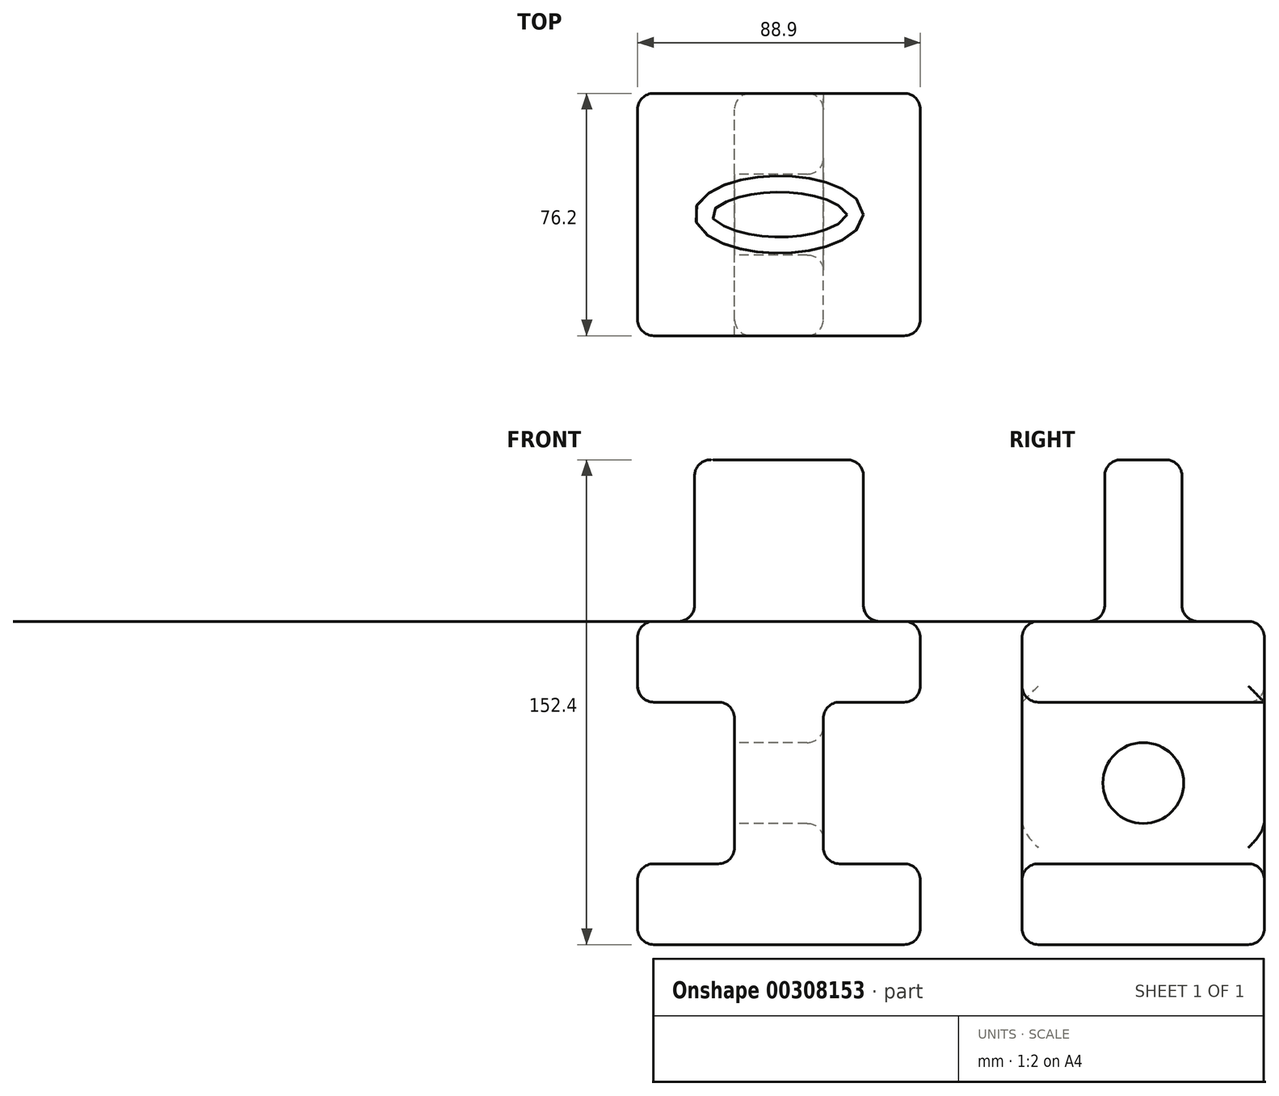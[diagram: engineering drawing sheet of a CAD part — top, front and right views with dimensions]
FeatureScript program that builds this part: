
annotation { "Feature Type Name" : "Feature", "Feature Type Description" : "" }
export const myFeature = defineFeature(function(context is Context, id is Id, definition is map)
    precondition{}
    {
        {
            var Q0;
            Q0=qCreatedBy(makeId("Front.planeOp"),FACE);
            var sketch = newSketch(context, id + "F0", { "sketchPlane" : qUnion([Q0])});
            skLineSegment(sketch, "E0", {"start": v(-56.03, -38.4) * mm, "end": v(32.87, -38.4) * mm});
            skLineSegment(sketch, "E1", {"start": v(32.87, -38.4) * mm, "end": v(32.87, -13) * mm});
            skLineSegment(sketch, "E2", {"start": v(32.87, -13) * mm, "end": v(2.39, -13) * mm});
            skLineSegment(sketch, "E3", {"start": v(2.39, -13) * mm, "end": v(2.39, 37.8) * mm});
            skLineSegment(sketch, "E4", {"start": v(2.39, 37.8) * mm, "end": v(32.87, 37.8) * mm});
            skLineSegment(sketch, "E5", {"start": v(32.87, 37.8) * mm, "end": v(32.87, 63.2) * mm});
            skLineSegment(sketch, "E6", {"start": v(32.87, 63.2) * mm, "end": v(-56.03, 63.2) * mm});
            skLineSegment(sketch, "E7", {"start": v(-56.03, 63.2) * mm, "end": v(-56.03, 37.8) * mm});
            skLineSegment(sketch, "E8", {"start": v(-56.03, 37.8) * mm, "end": v(-25.55, 37.8) * mm});
            skLineSegment(sketch, "E9", {"start": v(-25.55, 37.8) * mm, "end": v(-25.55, -13) * mm});
            skLineSegment(sketch, "E10", {"start": v(-25.55, -13) * mm, "end": v(-56.03, -13) * mm});
            skLineSegment(sketch, "E11", {"start": v(-56.03, -13) * mm, "end": v(-56.03, -38.4) * mm});
            skSolve(sketch);
        }
        {
            var Q0;
            Q0=makeQuery(id+"F0.imprint","IMPRINT",FACE,{"disambiguationData":[TD([[makeQuery(id+"F0.imprint","IMPRINT",EDGE,{"derivedFrom":sQuery(id+"F0.wireOp",EDGE,"E0")}),1.0]])]});
            extrude(context, id + "F1", {"entities" : qUnion([Q0]), "depth" : 76.2 * mm});
        }
        {
            var Q0;
            Q0=makeQuery(id+"F1.opExtrude","CAP_EDGE",EDGE,{"disambiguationData":[OSD([sQuery(id+"F0.wireOp",EDGE,"E6")])],"isStart":false});
            var Q1;
            Q1=makeQuery(id+"F1.opExtrude","SWEPT_EDGE",EDGE,{"disambiguationData":[OSD([sQuery(id+"F0.wireOp",EDGE,"E5"),sQuery(id+"F0.wireOp",EDGE,"E6")])]});
            var Q2;
            Q2=makeQuery(id+"F1.opExtrude","SWEPT_EDGE",EDGE,{"disambiguationData":[OSD([sQuery(id+"F0.wireOp",EDGE,"E4"),sQuery(id+"F0.wireOp",EDGE,"E5")])]});
            var Q3;
            Q3=makeQuery(id+"F1.opExtrude","CAP_EDGE",EDGE,{"disambiguationData":[OSD([sQuery(id+"F0.wireOp",EDGE,"E4")])],"isStart":false});
            var Q4;
            Q4=makeQuery(id+"F1.opExtrude","CAP_EDGE",EDGE,{"disambiguationData":[OSD([sQuery(id+"F0.wireOp",EDGE,"E3")])],"isStart":false});
            var Q5;
            Q5=makeQuery(id+"F1.opExtrude","CAP_EDGE",EDGE,{"disambiguationData":[OSD([sQuery(id+"F0.wireOp",EDGE,"E2")])],"isStart":false});
            var Q6;
            Q6=makeQuery(id+"F1.opExtrude","CAP_EDGE",EDGE,{"disambiguationData":[OSD([sQuery(id+"F0.wireOp",EDGE,"E1")])],"isStart":false});
            var Q7;
            Q7=makeQuery(id+"F1.opExtrude","CAP_EDGE",EDGE,{"disambiguationData":[OSD([sQuery(id+"F0.wireOp",EDGE,"E0")])],"isStart":false});
            var Q8;
            Q8=makeQuery(id+"F1.opExtrude","CAP_EDGE",EDGE,{"disambiguationData":[OSD([sQuery(id+"F0.wireOp",EDGE,"E11")])],"isStart":false});
            var Q9;
            Q9=makeQuery(id+"F1.opExtrude","CAP_EDGE",EDGE,{"disambiguationData":[OSD([sQuery(id+"F0.wireOp",EDGE,"E10")])],"isStart":false});
            var Q10;
            Q10=makeQuery(id+"F1.opExtrude","SWEPT_EDGE",EDGE,{"disambiguationData":[OSD([sQuery(id+"F0.wireOp",EDGE,"E1"),sQuery(id+"F0.wireOp",EDGE,"E2")])]});
            var Q11;
            Q11=makeQuery(id+"F1.opExtrude","SWEPT_FACE",FACE,{"disambiguationData":[OSD([sQuery(id+"F0.wireOp",EDGE,"E1")])]});
            var Q12;
            Q12=makeQuery(id+"F1.opExtrude","SWEPT_EDGE",EDGE,{"disambiguationData":[OSD([sQuery(id+"F0.wireOp",EDGE,"E2"),sQuery(id+"F0.wireOp",EDGE,"E3")])]});
            var Q13;
            Q13=makeQuery(id+"F1.opExtrude","CAP_EDGE",EDGE,{"disambiguationData":[OSD([sQuery(id+"F0.wireOp",EDGE,"E2")])],"isStart":true});
            var Q14;
            Q14=makeQuery(id+"F1.opExtrude","SWEPT_EDGE",EDGE,{"disambiguationData":[OSD([sQuery(id+"F0.wireOp",EDGE,"E3"),sQuery(id+"F0.wireOp",EDGE,"E4")])]});
            var Q15;
            Q15=makeQuery(id+"F1.opExtrude","CAP_EDGE",EDGE,{"disambiguationData":[OSD([sQuery(id+"F0.wireOp",EDGE,"E8")])],"isStart":true});
            var Q16;
            Q16=makeQuery(id+"F1.opExtrude","CAP_EDGE",EDGE,{"disambiguationData":[OSD([sQuery(id+"F0.wireOp",EDGE,"E9")])],"isStart":true});
            var Q17;
            Q17=makeQuery(id+"F1.opExtrude","SWEPT_EDGE",EDGE,{"disambiguationData":[OSD([sQuery(id+"F0.wireOp",EDGE,"E7"),sQuery(id+"F0.wireOp",EDGE,"E8")])]});
            var Q18;
            Q18=makeQuery(id+"F1.opExtrude","CAP_EDGE",EDGE,{"disambiguationData":[OSD([sQuery(id+"F0.wireOp",EDGE,"E6")])],"isStart":true});
            var Q19;
            Q19=makeQuery(id+"F1.opExtrude","CAP_EDGE",EDGE,{"disambiguationData":[OSD([sQuery(id+"F0.wireOp",EDGE,"E5")])],"isStart":true});
            var Q20;
            Q20=makeQuery(id+"F1.opExtrude","CAP_EDGE",EDGE,{"disambiguationData":[OSD([sQuery(id+"F0.wireOp",EDGE,"E5")])],"isStart":false});
            var Q21;
            Q21=makeQuery(id+"F1.opExtrude","CAP_EDGE",EDGE,{"disambiguationData":[OSD([sQuery(id+"F0.wireOp",EDGE,"E7")])],"isStart":true});
            var Q22;
            Q22=makeQuery(id+"F1.opExtrude","CAP_EDGE",EDGE,{"disambiguationData":[OSD([sQuery(id+"F0.wireOp",EDGE,"E11")])],"isStart":true});
            var Q23;
            Q23=makeQuery(id+"F1.opExtrude","CAP_EDGE",EDGE,{"disambiguationData":[OSD([sQuery(id+"F0.wireOp",EDGE,"E0")])],"isStart":true});
            var Q24;
            Q24=makeQuery(id+"F1.opExtrude","CAP_EDGE",EDGE,{"disambiguationData":[OSD([sQuery(id+"F0.wireOp",EDGE,"E10")])],"isStart":true});
            var Q25;
            Q25=makeQuery(id+"F1.opExtrude","SWEPT_EDGE",EDGE,{"disambiguationData":[OSD([sQuery(id+"F0.wireOp",EDGE,"E0"),sQuery(id+"F0.wireOp",EDGE,"E11")])]});
            var Q26;
            Q26=makeQuery(id+"F1.opExtrude","SWEPT_EDGE",EDGE,{"disambiguationData":[OSD([sQuery(id+"F0.wireOp",EDGE,"E8"),sQuery(id+"F0.wireOp",EDGE,"E9")])]});
            var Q27;
            Q27=makeQuery(id+"F1.opExtrude","SWEPT_EDGE",EDGE,{"disambiguationData":[OSD([sQuery(id+"F0.wireOp",EDGE,"E9"),sQuery(id+"F0.wireOp",EDGE,"E10")])]});
            var Q28;
            Q28=makeQuery(id+"F1.opExtrude","SWEPT_EDGE",EDGE,{"disambiguationData":[OSD([sQuery(id+"F0.wireOp",EDGE,"E10"),sQuery(id+"F0.wireOp",EDGE,"E11")])]});
            var Q29;
            Q29=makeQuery(id+"F1.opExtrude","SWEPT_EDGE",EDGE,{"disambiguationData":[OSD([sQuery(id+"F0.wireOp",EDGE,"E6"),sQuery(id+"F0.wireOp",EDGE,"E7")])]});
            var Q30;
            Q30=makeQuery(id+"F1.opExtrude","CAP_EDGE",EDGE,{"disambiguationData":[OSD([sQuery(id+"F0.wireOp",EDGE,"E7")])],"isStart":false});
            fillet(context, id + "F2", {"entities" : qUnion([Q0, Q1, Q2, Q3, Q4, Q5, Q6, Q7, Q8, Q9, Q10, Q11, Q12, Q13, Q14, Q15, Q16, Q17, Q18, Q19, Q20, Q21, Q22, Q23, Q24, Q25, Q26, Q27, Q28, Q29, Q30]), "radius" : 5.08 * mm, "tangentPropagation" : true, "allowEdgeOverflow" : false});
        }
        {
            var Q0;
            Q0=makeQuery(id+"F1.opExtrude","SWEPT_FACE",FACE,{"disambiguationData":[OSD([sQuery(id+"F0.wireOp",EDGE,"E9")])]});
            var sketch = newSketch(context, id + "F3", { "sketchPlane" : qUnion([Q0])});
            skCircle(sketch, "E12", {"center": v(38.1, 12.4) * mm, "radius": 12.7 * mm});
            skPoint(sketch, "E12.centerSnap0", {"position": v(38.1, 32.72) * mm});
            skPoint(sketch, "E12.centerSnap1", {"position": v(5.08, 12.4) * mm});
            skSolve(sketch);
        }
        {
            var Q0;
            Q0=makeQuery(id+"F3.imprint","IMPRINT",FACE,{"disambiguationData":[TD([[makeQuery(id+"F3.imprint","IMPRINT",EDGE,{"derivedFrom":sQuery(id+"F3.wireOp",EDGE,"E12")}),1.0]])]});
            extrude(context, id + "F4", {"entities" : qUnion([Q0]), "operationType" : NewBodyOperationType.REMOVE, "oppositeDirection" : true, "depth" : 101.6 * mm});
        }
        {
            var Q0;
            Q0=makeQuery(id+"F1.opExtrude","SWEPT_FACE",FACE,{"disambiguationData":[OSD([sQuery(id+"F0.wireOp",EDGE,"E6")])]});
            var sketch = newSketch(context, id + "F5", { "sketchPlane" : qUnion([Q0])});
            skEllipse(sketch, "E13", {"center": v(-11.58, -38.1) * mm, "majorRadius": 26.56 * mm, "minorRadius": 12.15 * mm, "majorAxis": v(1, 0)});
            skPoint(sketch, "E13.centerSnap0", {"position": v(27.79, -38.1) * mm});
            skPoint(sketch, "E13.centerSnap1", {"position": v(-11.58, -5.08) * mm});
            skSolve(sketch);
        }
        {
            var Q0;
            Q0=makeQuery(id+"F5.imprint","IMPRINT",FACE,{"disambiguationData":[TD([[makeQuery(id+"F5.imprint","IMPRINT",EDGE,{"derivedFrom":sQuery(id+"F5.wireOp",EDGE,"E13")}),1.0]])]});
            extrude(context, id + "F6", {"entities" : qUnion([Q0]), "operationType" : NewBodyOperationType.ADD, "depth" : 50.8 * mm});
        }
        {
            var Q0;
            Q0=makeQuery(id+"F6.opExtrude","CAP_EDGE",EDGE,{"disambiguationData":[OSD([sQuery(id+"F5.wireOp",EDGE,"E13")])],"isStart":false});
            var Q1;
            Q1=makeQuery(id+"F6.opExtrude","SWEPT_FACE",FACE,{"disambiguationData":[OSD([sQuery(id+"F5.wireOp",EDGE,"E13")])]});
            var Q2;
            Q2=makeQuery(id+"F4.boolean.opBoolean","INTERSECT",EDGE,{"derivedFrom":[makeQuery(id+"F1.opExtrude","SWEPT_FACE",FACE,{"disambiguationData":[OSD([sQuery(id+"F0.wireOp",EDGE,"E3")])]}),makeQuery(id+"F4.opExtrude","SWEPT_FACE",FACE,{"disambiguationData":[OSD([sQuery(id+"F3.wireOp",EDGE,"E12")])]})]});
            var Q3;
            Q3=makeQuery(id+"F4.boolean.opBoolean","COPY",EDGE,{"derivedFrom":makeQuery(id+"F4.opExtrude","CAP_EDGE",EDGE,{"disambiguationData":[OSD([sQuery(id+"F3.wireOp",EDGE,"E12")])],"isStart":true})});
            fillet(context, id + "F7", {"entities" : qUnion([Q0, Q1, Q2, Q3]), "radius" : 5.08 * mm, "tangentPropagation" : true, "allowEdgeOverflow" : false});
        }
    });
